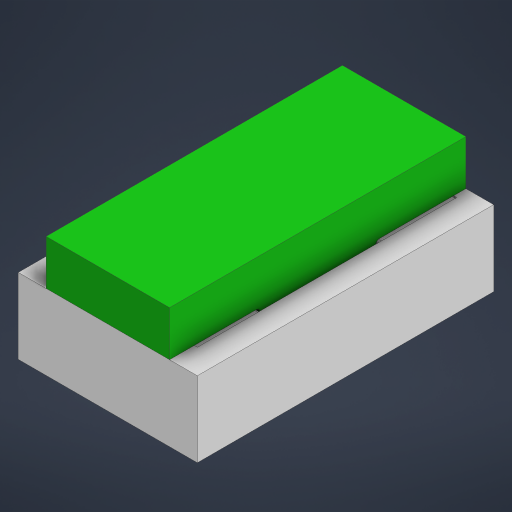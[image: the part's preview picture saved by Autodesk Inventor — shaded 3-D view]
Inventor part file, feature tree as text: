
AUTODESK INVENTOR PART (.ipt)
format: ipt  version: 2024.3 (Build 283343010, 343A)  size: 404,992 bytes
history: native  units: mm
features: extrude x3, sketch x2
ambient origin geometry x8: Origin, YZ Plane, XZ Plane, XY Plane, X Axis, Y Axis, Z Axis, Center Point
bodies: Volumenkörper4 (feature_tree)
feature tree (5):
  sketch  "Skizze3"  dims[d13=24.0mm d14=6.0mm]
  extrude  "Extrusion2"  Depth=6.0mm
  extrude  "Extrusion3"  Depth=0.1mm
  extrude  "Extrusion4"  Depth=1.0mm
  sketch  "Skizze4"  dims[d17=2.0mm d18=0.1mm d19=1.0mm d20=0.1mm d21=10.5mm d22=0.0mm d24=2.0mm d25=24.0mm d26=0.0mm d27=10.0mm d28=2.0mm d29=0.0mm d30=0.0mm d31=2.0mm]
